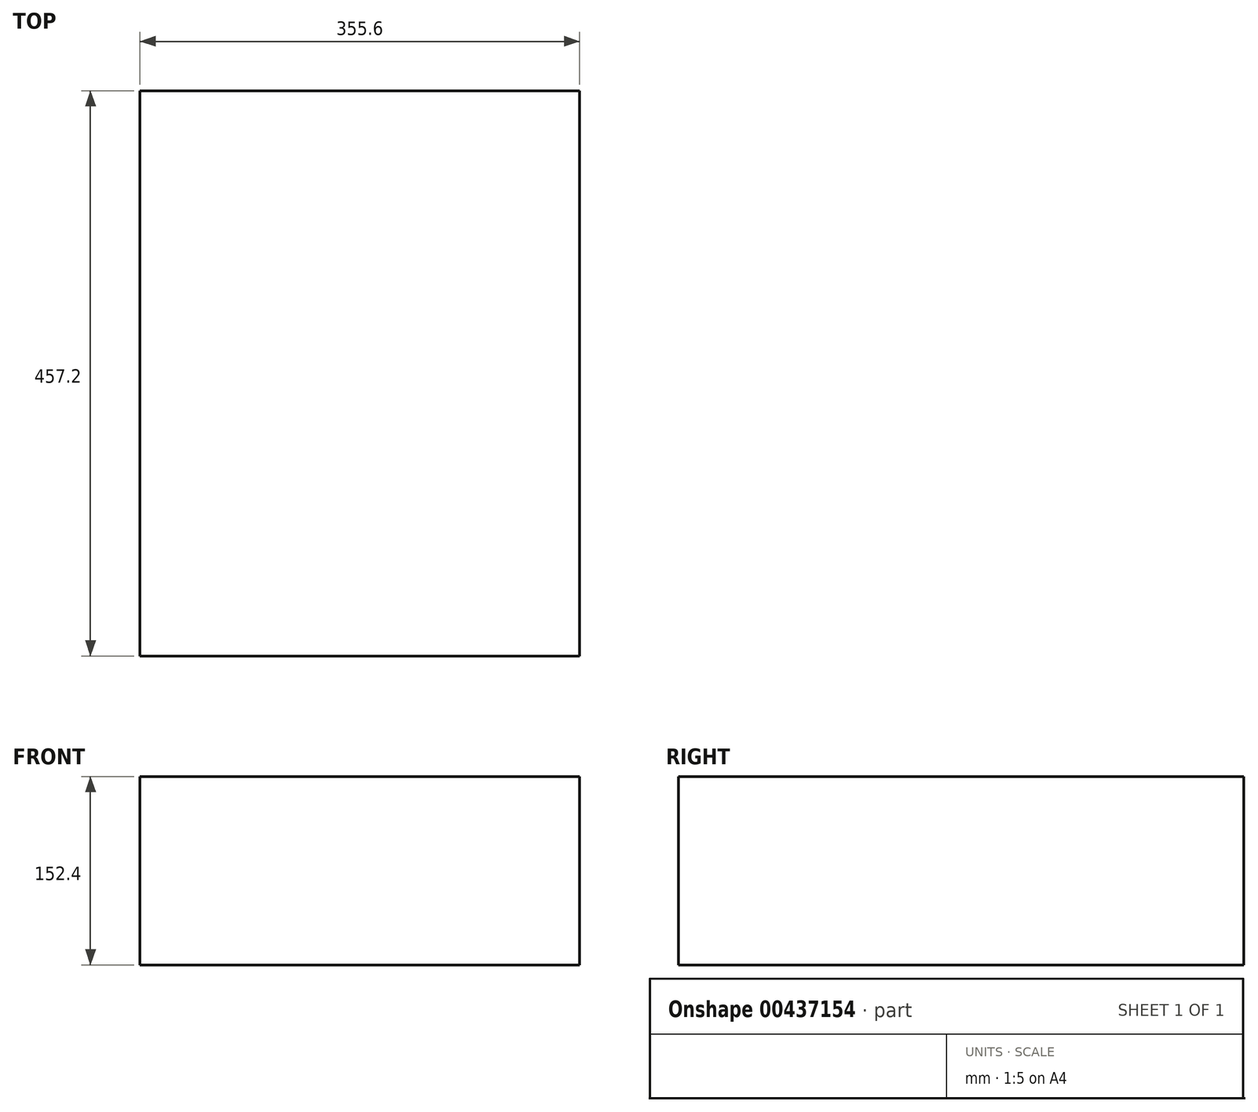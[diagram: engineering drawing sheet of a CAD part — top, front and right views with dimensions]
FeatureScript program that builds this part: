
annotation { "Feature Type Name" : "Feature", "Feature Type Description" : "" }
export const myFeature = defineFeature(function(context is Context, id is Id, definition is map)
    precondition{}
    {
        {
            var Q0;
            Q0=qCreatedBy(makeId("Front.planeOp"),FACE);
            var sketch = newSketch(context, id + "F0", { "sketchPlane" : qUnion([Q0])});
            skLineSegment(sketch, "E0.bottom", {"start": v(0, 0) * mm, "end": v(-355.6, 0) * mm});
            skLineSegment(sketch, "E0.top", {"start": v(0, 152.4) * mm, "end": v(-355.6, 152.4) * mm});
            skLineSegment(sketch, "E0.left", {"start": v(0, 0) * mm, "end": v(0, 152.4) * mm});
            skLineSegment(sketch, "E0.right", {"start": v(-355.6, 0) * mm, "end": v(-355.6, 152.4) * mm});
            skSolve(sketch);
        }
        {
            var Q0;
            Q0 = qSketchRegion(id + "F0", true);
            extrude(context, id + "F1", {"entities" : qUnion([Q0]), "depth" : 457.2 * mm});
        }
    });
